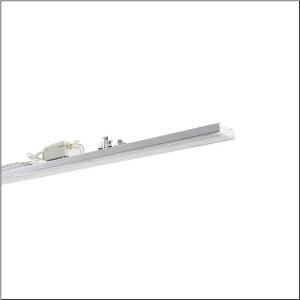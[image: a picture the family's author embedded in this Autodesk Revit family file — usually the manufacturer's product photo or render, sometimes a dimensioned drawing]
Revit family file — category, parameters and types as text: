
# Revit family: licross_r__21_recessed_mo_52tl12mn4a5g_9149
name_source: partatom
category: Lighting Fixtures
units: mm (PartAtom-declared; Revit-internal decimal feet)

## family parameters
Cut with Voids When Loaded = No
Host = Face
Light Source = No
Part Type = Normal
Room Calculation Point = No
Round Connector Dimension = Use Diameter
Shared = No

## types (1)
- --- (1 x LED, 10990 lm, 60.5 W, 4000K)
    Apparent Load = 61 VA
    CIE Flux Codes = 72 92 99 100 100
    Color Rendering = 80
    Color Temperature = 4000K
    Default Elevation = 1800 mm
    Description = Licross® 21 Recessed MO, luminaire insert, of sheet steel, galvanised, coil coated, white, length: 1.500mm, width: 66mm, height: 67mm, LED rated luminous flux: 10.990lm, light colour: 840, control gear: ON/OFF Multilumen, with plug, 3-pole, with phase selection, mains connection: 220..240V, AC, 50/60Hz, rated input power: 61W, halogen-free wiring, primary optical cover: cover, of PMMA, light emission: direct distribution, primary light characteristic: symmetric, protection rating (complete): IP40, insulation class (complete): insulation class I (protective earthing), certification: CE, ENEC, VDE, UKCA, protection symbol: D if used in an environment without relevant dust loads with corresponding accessories, impact resistance: IK06, permissible ambient temperature for indoor applications: -35..+40°C, corresponds to IFS (International Featured Standards) requirements for safety and quality in the food industry, reducing of maximum allowable ambient temperature of 5°C with ceiling mounting, LABS conformity tested according to VDMA 24364:2018-05, packaging unit: 1 piece
    Height = 58 mm
    Lamp = 1 x LED
    Lamp Light Flux = 10990 lm
    Lamp Power = 60.5 W
    Lamp count = 1
    Length = 1500 mm
    Luminous efficacy = 182 lm/W
    Manufacturer = Siteco
    ModVariant = No
    Model = 52TL12MN4A5G
    Mounting Place = Ceiling
    Mounting Type = Pendant
    Number of Poles = 1
    OnlyDefault = Yes
    Power Factor = 1
    Product Name = Licross® 21 Recessed MO
    Product group = luminaire insert
    ProductGroupID = 901
    Protection Class = Protection class I
    Protection Degree = IP 40
    RLX_Detail_Level = 1
    RLX_Emergency_Light_Flux = 0 lm
    RLX_Emergency_Type = 0
    RLX_Emergency_Type_DB = No
    RlxData = <blob elided: 22297 chars, md5=cda5a906>
    Socket = socket
    Standby Power = 0 W
    System Light Flux = 10990 lm
    System Power = 61 W
    Type Comments = factory setting: luminous flux: 100 % | (A | C | E) | 140 mA
    Type Image = l_1296930.jpg
    URL = http://relux.com
    VarID = @adj_038145
    Voltage = 0 V
    Weight = 0.00 kg
    Width = 66 mm

## geometry (parser evidence)
native form markers: Blend x4, Sweep x11
no freeform markers — native parametric forms only
